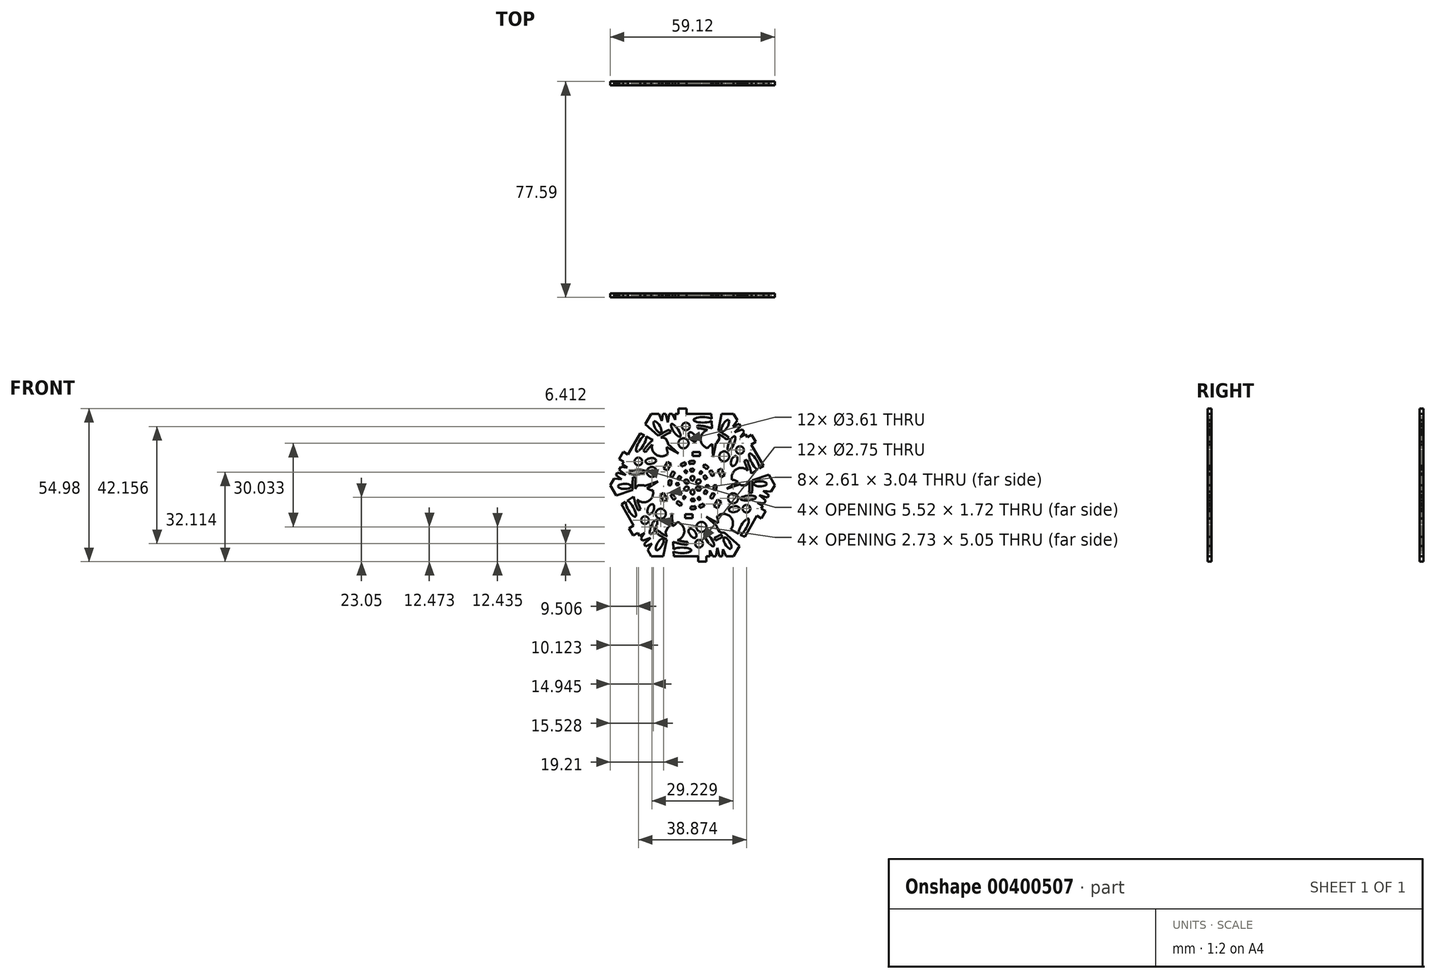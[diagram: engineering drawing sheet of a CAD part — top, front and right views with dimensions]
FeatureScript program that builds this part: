
annotation { "Feature Type Name" : "Feature", "Feature Type Description" : "" }
export const myFeature = defineFeature(function(context is Context, id is Id, definition is map)
    precondition{}
    {
        {
            var Q0;
            Q0=qCreatedBy(makeId("Front.planeOp"),FACE);
            var sketch = newSketch(context, id + "F0", { "sketchPlane" : qUnion([Q0])});
            skLineSegment(sketch, "E0", {"start": v(0, 0) * mm, "end": v(-15.64, -27.08) * mm});
            skLineSegment(sketch, "E1", {"start": v(-29.56, -51.2) * mm, "end": v(4.14, -51.2) * mm});
            skLineSegment(sketch, "E2", {"start": v(29.56, -51.2) * mm, "end": v(17.4, -30.14) * mm});
            skArc(sketch, "E3", {"start": v(-19.34, -33.5) * mm, "mid": v(-6.77, -36.48) * mm, "end": v(-15.64, -27.08) * mm});
            skArc(sketch, "E4", {"start": v(17.4, -30.14) * mm, "mid": v(17.43, -22.72) * mm, "end": v(10.99, -19.03) * mm});
            skLineSegment(sketch, "E5.top", {"start": v(4.14, -54.98) * mm, "end": v(10.05, -54.98) * mm});
            skLineSegment(sketch, "E5.left", {"start": v(4.14, -51.2) * mm, "end": v(4.14, -54.98) * mm});
            skLineSegment(sketch, "E5.right", {"start": v(10.05, -51.2) * mm, "end": v(10.05, -54.98) * mm});
            skLineSegment(sketch, "E6.bottom", {"start": v(-5.32, -20.89) * mm, "end": v(0, -20.89) * mm});
            skLineSegment(sketch, "E6.top", {"start": v(-5.32, -23.85) * mm, "end": v(0, -23.85) * mm});
            skLineSegment(sketch, "E6.left", {"start": v(-5.32, -20.89) * mm, "end": v(-5.32, -23.85) * mm});
            skLineSegment(sketch, "E6.right", {"start": v(0, -20.89) * mm, "end": v(0, -23.85) * mm});
            skLineSegment(sketch, "E7.trimOffspring", {"start": v(-19.34, -33.5) * mm, "end": v(-29.56, -51.2) * mm});
            skLineSegment(sketch, "E8.trimOffspring", {"start": v(10.99, -19.03) * mm, "end": v(0, 0) * mm});
            skLineSegment(sketch, "E9.trimOffspring", {"start": v(10.05, -51.2) * mm, "end": v(29.56, -51.2) * mm});
            skArc(sketch, "E10.1.0", {"start": v(19.34, -33.5) * mm, "mid": v(28.2, -24.1) * mm, "end": v(15.64, -27.08) * mm});
            skLineSegment(sketch, "E10.1.1", {"start": v(15.43, -15.05) * mm, "end": v(18.1, -10.44) * mm});
            skArc(sketch, "E10.1.2", {"start": v(34.8, 0) * mm, "mid": v(28.39, 3.73) * mm, "end": v(21.97, 0) * mm});
            skLineSegment(sketch, "E10.1.3", {"start": v(49.69, -23.9) * mm, "end": v(52.64, -18.79) * mm});
            skLineSegment(sketch, "E10.1.4", {"start": v(59.12, 0) * mm, "end": v(34.8, 0) * mm});
            skLineSegment(sketch, "E10.1.5", {"start": v(29.56, -51.2) * mm, "end": v(46.4, -22.02) * mm});
            skLineSegment(sketch, "E10.1.6", {"start": v(0, 0) * mm, "end": v(15.64, -27.08) * mm});
            skLineSegment(sketch, "E10.1.7", {"start": v(18, -16.53) * mm, "end": v(20.65, -11.92) * mm});
            skLineSegment(sketch, "E10.1.8", {"start": v(19.34, -33.5) * mm, "end": v(29.56, -51.2) * mm});
            skLineSegment(sketch, "E10.1.9", {"start": v(49.37, -16.9) * mm, "end": v(59.12, 0) * mm});
            skLineSegment(sketch, "E10.1.10", {"start": v(21.97, 0) * mm, "end": v(0, 0) * mm});
            skLineSegment(sketch, "E10.1.11", {"start": v(46.4, -22.02) * mm, "end": v(49.69, -23.9) * mm});
            skLineSegment(sketch, "E10.1.12", {"start": v(49.37, -16.9) * mm, "end": v(52.64, -18.79) * mm});
            skLineSegment(sketch, "E10.1.13", {"start": v(15.43, -15.05) * mm, "end": v(18, -16.53) * mm});
            skLineSegment(sketch, "E10.1.14", {"start": v(18.1, -10.44) * mm, "end": v(20.65, -11.92) * mm});
            skArc(sketch, "E10.2.0", {"start": v(38.68, 0) * mm, "mid": v(34.98, 12.37) * mm, "end": v(31.27, 0) * mm});
            skLineSegment(sketch, "E10.2.1", {"start": v(20.75, 5.84) * mm, "end": v(18.1, 10.44) * mm});
            skArc(sketch, "E10.2.2", {"start": v(17.4, 30.14) * mm, "mid": v(10.96, 26.45) * mm, "end": v(10.99, 19.03) * mm});
            skLineSegment(sketch, "E10.2.3", {"start": v(45.55, 31.08) * mm, "end": v(42.6, 36.2) * mm});
            skLineSegment(sketch, "E10.2.4", {"start": v(29.56, 51.2) * mm, "end": v(17.4, 30.14) * mm});
            skLineSegment(sketch, "E10.2.5", {"start": v(59.12, 0) * mm, "end": v(42.27, 29.18) * mm});
            skLineSegment(sketch, "E10.2.6", {"start": v(0, 0) * mm, "end": v(31.27, 0) * mm});
            skLineSegment(sketch, "E10.2.7", {"start": v(23.31, 7.31) * mm, "end": v(20.65, 11.92) * mm});
            skLineSegment(sketch, "E10.2.8", {"start": v(38.68, 0) * mm, "end": v(59.12, 0) * mm});
            skLineSegment(sketch, "E10.2.9", {"start": v(39.32, 34.3) * mm, "end": v(29.56, 51.2) * mm});
            skLineSegment(sketch, "E10.2.10", {"start": v(10.99, 19.03) * mm, "end": v(0, 0) * mm});
            skLineSegment(sketch, "E10.2.11", {"start": v(42.27, 29.18) * mm, "end": v(45.55, 31.08) * mm});
            skLineSegment(sketch, "E10.2.12", {"start": v(39.32, 34.3) * mm, "end": v(42.6, 36.2) * mm});
            skLineSegment(sketch, "E10.2.13", {"start": v(20.75, 5.84) * mm, "end": v(23.31, 7.31) * mm});
            skLineSegment(sketch, "E10.2.14", {"start": v(18.1, 10.44) * mm, "end": v(20.65, 11.92) * mm});
            skArc(sketch, "E10.3.0", {"start": v(19.34, 33.5) * mm, "mid": v(6.77, 36.48) * mm, "end": v(15.64, 27.08) * mm});
            skLineSegment(sketch, "E10.3.1", {"start": v(5.32, 20.89) * mm, "end": v(0, 20.89) * mm});
            skArc(sketch, "E10.3.2", {"start": v(-17.4, 30.14) * mm, "mid": v(-17.43, 22.72) * mm, "end": v(-10.99, 19.03) * mm});
            skLineSegment(sketch, "E10.3.3", {"start": v(-4.14, 54.98) * mm, "end": v(-10.05, 54.98) * mm});
            skLineSegment(sketch, "E10.3.4", {"start": v(-29.56, 51.2) * mm, "end": v(-17.4, 30.14) * mm});
            skLineSegment(sketch, "E10.3.5", {"start": v(29.56, 51.2) * mm, "end": v(-4.14, 51.2) * mm});
            skLineSegment(sketch, "E10.3.6", {"start": v(0, 0) * mm, "end": v(15.64, 27.08) * mm});
            skLineSegment(sketch, "E10.3.7", {"start": v(5.32, 23.85) * mm, "end": v(0, 23.85) * mm});
            skLineSegment(sketch, "E10.3.8", {"start": v(19.34, 33.5) * mm, "end": v(29.56, 51.2) * mm});
            skLineSegment(sketch, "E10.3.9", {"start": v(-10.05, 51.2) * mm, "end": v(-29.56, 51.2) * mm});
            skLineSegment(sketch, "E10.3.10", {"start": v(-10.99, 19.03) * mm, "end": v(0, 0) * mm});
            skLineSegment(sketch, "E10.3.11", {"start": v(-4.14, 51.2) * mm, "end": v(-4.14, 54.98) * mm});
            skLineSegment(sketch, "E10.3.12", {"start": v(-10.05, 51.2) * mm, "end": v(-10.05, 54.98) * mm});
            skLineSegment(sketch, "E10.3.13", {"start": v(5.32, 20.89) * mm, "end": v(5.32, 23.85) * mm});
            skLineSegment(sketch, "E10.3.14", {"start": v(0, 20.89) * mm, "end": v(0, 23.85) * mm});
            skArc(sketch, "E10.4.0", {"start": v(-19.34, 33.5) * mm, "mid": v(-28.2, 24.1) * mm, "end": v(-15.64, 27.08) * mm});
            skLineSegment(sketch, "E10.4.1", {"start": v(-15.43, 15.05) * mm, "end": v(-18.1, 10.44) * mm});
            skArc(sketch, "E10.4.2", {"start": v(-34.8, 0) * mm, "mid": v(-28.39, -3.73) * mm, "end": v(-21.97, 0) * mm});
            skLineSegment(sketch, "E10.4.3", {"start": v(-49.69, 23.9) * mm, "end": v(-52.64, 18.79) * mm});
            skLineSegment(sketch, "E10.4.4", {"start": v(-59.12, 0) * mm, "end": v(-34.8, 0) * mm});
            skLineSegment(sketch, "E10.4.5", {"start": v(-29.56, 51.2) * mm, "end": v(-46.4, 22.02) * mm});
            skLineSegment(sketch, "E10.4.6", {"start": v(0, 0) * mm, "end": v(-15.64, 27.08) * mm});
            skLineSegment(sketch, "E10.4.7", {"start": v(-18, 16.53) * mm, "end": v(-20.65, 11.92) * mm});
            skLineSegment(sketch, "E10.4.8", {"start": v(-19.34, 33.5) * mm, "end": v(-29.56, 51.2) * mm});
            skLineSegment(sketch, "E10.4.9", {"start": v(-49.37, 16.9) * mm, "end": v(-59.12, 0) * mm});
            skLineSegment(sketch, "E10.4.10", {"start": v(-21.97, 0) * mm, "end": v(0, 0) * mm});
            skLineSegment(sketch, "E10.4.11", {"start": v(-46.4, 22.02) * mm, "end": v(-49.69, 23.9) * mm});
            skLineSegment(sketch, "E10.4.12", {"start": v(-49.37, 16.9) * mm, "end": v(-52.64, 18.79) * mm});
            skLineSegment(sketch, "E10.4.13", {"start": v(-15.43, 15.05) * mm, "end": v(-18, 16.53) * mm});
            skLineSegment(sketch, "E10.4.14", {"start": v(-18.1, 10.44) * mm, "end": v(-20.65, 11.92) * mm});
            skArc(sketch, "E10.5.0", {"start": v(-38.68, 0) * mm, "mid": v(-34.98, -12.37) * mm, "end": v(-31.27, 0) * mm});
            skLineSegment(sketch, "E10.5.1", {"start": v(-20.75, -5.84) * mm, "end": v(-18.1, -10.44) * mm});
            skArc(sketch, "E10.5.2", {"start": v(-17.4, -30.14) * mm, "mid": v(-10.96, -26.45) * mm, "end": v(-10.99, -19.03) * mm});
            skLineSegment(sketch, "E10.5.3", {"start": v(-45.55, -31.08) * mm, "end": v(-42.6, -36.2) * mm});
            skLineSegment(sketch, "E10.5.4", {"start": v(-29.56, -51.2) * mm, "end": v(-17.4, -30.14) * mm});
            skLineSegment(sketch, "E10.5.5", {"start": v(-59.12, 0) * mm, "end": v(-42.27, -29.18) * mm});
            skLineSegment(sketch, "E10.5.6", {"start": v(0, 0) * mm, "end": v(-31.27, 0) * mm});
            skLineSegment(sketch, "E10.5.7", {"start": v(-23.31, -7.31) * mm, "end": v(-20.65, -11.92) * mm});
            skLineSegment(sketch, "E10.5.8", {"start": v(-38.68, 0) * mm, "end": v(-59.12, 0) * mm});
            skLineSegment(sketch, "E10.5.9", {"start": v(-39.32, -34.3) * mm, "end": v(-29.56, -51.2) * mm});
            skLineSegment(sketch, "E10.5.10", {"start": v(-10.99, -19.03) * mm, "end": v(0, 0) * mm});
            skLineSegment(sketch, "E10.5.11", {"start": v(-42.27, -29.18) * mm, "end": v(-45.55, -31.08) * mm});
            skLineSegment(sketch, "E10.5.12", {"start": v(-39.32, -34.3) * mm, "end": v(-42.6, -36.2) * mm});
            skLineSegment(sketch, "E10.5.13", {"start": v(-20.75, -5.84) * mm, "end": v(-23.31, -7.31) * mm});
            skLineSegment(sketch, "E10.5.14", {"start": v(-18.1, -10.44) * mm, "end": v(-20.65, -11.92) * mm});
            skPoint(sketch, "E10.center", {"position": v(0, 0) * mm});
            skSolve(sketch);
        }
        {
            var Q0;
            Q0=makeQuery(id+"F0.imprint","IMPRINT",FACE,{"disambiguationData":[TD([[makeQuery(id+"F0.imprint","IMPRINT",EDGE,{"derivedFrom":sQuery(id+"F0.wireOp",EDGE,"E10.4.1")}),1.0]])]});
            var Q1;
            Q1=makeQuery(id+"F0.imprint","IMPRINT",FACE,{"disambiguationData":[TD([[makeQuery(id+"F0.imprint","IMPRINT",EDGE,{"derivedFrom":sQuery(id+"F0.wireOp",EDGE,"E10.1.1")}),1.0]])]});
            var Q2;
            {var subQ0=sQuery(id+"F0.wireOp",EDGE,"E1");Q2=makeQuery(id+"F0.imprint","IMPRINT",FACE,{"disambiguationData":[TD([[makeQuery(id+"F0.imprint","IMPRINT",EDGE,{"derivedFrom":subQ0}),1.0]])]});}
            var Q3;
            Q3=makeQuery(id+"F0.imprint","IMPRINT",FACE,{"disambiguationData":[TD([[makeQuery(id+"F0.imprint","IMPRINT",EDGE,{"derivedFrom":sQuery(id+"F0.wireOp",EDGE,"E10.2.1")}),1.0]])]});
            var Q4;
            Q4=makeQuery(id+"F0.imprint","IMPRINT",FACE,{"disambiguationData":[TD([[makeQuery(id+"F0.imprint","IMPRINT",EDGE,{"derivedFrom":sQuery(id+"F0.wireOp",EDGE,"E10.3.1")}),1.0]])]});
            var Q5;
            {var subQ0=sQuery(id+"F0.wireOp",EDGE,"E10.4.6");var subQ1=sQuery(id+"F0.wireOp",EDGE,"E10.3.2");var subQ2=makeQuery(id+"F0.imprint","INTERSECT",VERTEX,{"derivedFrom":[subQ1,subQ0]});Q5=makeQuery(id+"F0.imprint","IMPRINT",FACE,{"disambiguationData":[TD([[makeQuery(id+"F0.imprint","IMPRINT",EDGE,{"disambiguationData":[TD([[subQ2,1.0]])],"derivedFrom":subQ1}),1.0]])]});}
            var Q6;
            {var subQ0=sQuery(id+"F0.wireOp",EDGE,"E10.3.6");var subQ1=sQuery(id+"F0.wireOp",EDGE,"E10.2.2");var subQ2=makeQuery(id+"F0.imprint","INTERSECT",VERTEX,{"derivedFrom":[subQ1,subQ0]});Q6=makeQuery(id+"F0.imprint","IMPRINT",FACE,{"disambiguationData":[TD([[makeQuery(id+"F0.imprint","IMPRINT",EDGE,{"disambiguationData":[TD([[subQ2,1.0]])],"derivedFrom":subQ1}),1.0]])]});}
            var Q7;
            {var subQ0=sQuery(id+"F0.wireOp",EDGE,"E0");Q7=makeQuery(id+"F0.imprint","IMPRINT",FACE,{"disambiguationData":[TD([[makeQuery(id+"F0.imprint","IMPRINT",EDGE,{"derivedFrom":subQ0}),1.0]])]});}
            var Q8;
            {var subQ0=sQuery(id+"F0.wireOp",EDGE,"E10.1.6");var subQ1=sQuery(id+"F0.wireOp",EDGE,"E4");var subQ2=makeQuery(id+"F0.imprint","INTERSECT",VERTEX,{"derivedFrom":[subQ1,subQ0]});Q8=makeQuery(id+"F0.imprint","IMPRINT",FACE,{"disambiguationData":[TD([[makeQuery(id+"F0.imprint","IMPRINT",EDGE,{"disambiguationData":[TD([[subQ2,1.0]])],"derivedFrom":subQ1}),1.0]])]});}
            var Q9;
            {var subQ0=sQuery(id+"F0.wireOp",EDGE,"E10.2.6");var subQ1=sQuery(id+"F0.wireOp",EDGE,"E10.1.2");var subQ2=makeQuery(id+"F0.imprint","INTERSECT",VERTEX,{"derivedFrom":[subQ1,subQ0]});Q9=makeQuery(id+"F0.imprint","IMPRINT",FACE,{"disambiguationData":[TD([[makeQuery(id+"F0.imprint","IMPRINT",EDGE,{"disambiguationData":[TD([[subQ2,1.0]])],"derivedFrom":subQ1}),1.0]])]});}
            var Q10;
            {var subQ0=sQuery(id+"F0.wireOp",EDGE,"E10.5.6");var subQ1=sQuery(id+"F0.wireOp",EDGE,"E10.4.2");var subQ2=makeQuery(id+"F0.imprint","INTERSECT",VERTEX,{"derivedFrom":[subQ1,subQ0]});Q10=makeQuery(id+"F0.imprint","IMPRINT",FACE,{"disambiguationData":[TD([[makeQuery(id+"F0.imprint","IMPRINT",EDGE,{"disambiguationData":[TD([[subQ2,1.0]])],"derivedFrom":subQ1}),1.0]])]});}
            var Q11;
            {var subQ7=sQuery(id+"F0.wireOp",EDGE,"E0");Q11=makeQuery(id+"F0.imprint","IMPRINT",FACE,{"disambiguationData":[TD([[makeQuery(id+"F0.imprint","IMPRINT",EDGE,{"derivedFrom":subQ7}),-1.0]])]});}
            extrude(context, id + "F1", {"entities" : qUnion([Q0, Q1, Q2, Q3, Q4, Q5, Q6, Q7, Q8, Q9, Q10, Q11]), "depth" : 2.8 * mm});
        }
        {
            var Q0;
            Q0=makeQuery(id+"F1.opExtrude","CAP_FACE",FACE,{"disambiguationData":[OSD([sQuery(id+"F0.wireOp",EDGE,"E1"),sQuery(id+"F0.wireOp",EDGE,"E2"),sQuery(id+"F0.wireOp",EDGE,"E3"),sQuery(id+"F0.wireOp",EDGE,"E4"),sQuery(id+"F0.wireOp",EDGE,"E5.top"),sQuery(id+"F0.wireOp",EDGE,"E5.left"),sQuery(id+"F0.wireOp",EDGE,"E5.right"),sQuery(id+"F0.wireOp",EDGE,"E6.bottom"),sQuery(id+"F0.wireOp",EDGE,"E6.top"),sQuery(id+"F0.wireOp",EDGE,"E6.left"),sQuery(id+"F0.wireOp",EDGE,"E6.right"),sQuery(id+"F0.wireOp",EDGE,"E9.trimOffspring"),sQuery(id+"F0.wireOp",EDGE,"E10.1.0"),sQuery(id+"F0.wireOp",EDGE,"E10.1.1"),sQuery(id+"F0.wireOp",EDGE,"E10.1.2"),sQuery(id+"F0.wireOp",EDGE,"E10.1.3"),sQuery(id+"F0.wireOp",EDGE,"E10.1.4"),sQuery(id+"F0.wireOp",EDGE,"E10.1.5"),sQuery(id+"F0.wireOp",EDGE,"E10.1.7"),sQuery(id+"F0.wireOp",EDGE,"E10.1.9"),sQuery(id+"F0.wireOp",EDGE,"E10.1.11"),sQuery(id+"F0.wireOp",EDGE,"E10.1.12"),sQuery(id+"F0.wireOp",EDGE,"E10.1.13"),sQuery(id+"F0.wireOp",EDGE,"E10.1.14"),sQuery(id+"F0.wireOp",EDGE,"E10.2.0"),sQuery(id+"F0.wireOp",EDGE,"E10.2.1"),sQuery(id+"F0.wireOp",EDGE,"E10.2.2"),sQuery(id+"F0.wireOp",EDGE,"E10.2.3"),sQuery(id+"F0.wireOp",EDGE,"E10.2.4"),sQuery(id+"F0.wireOp",EDGE,"E10.2.5"),sQuery(id+"F0.wireOp",EDGE,"E10.2.7"),sQuery(id+"F0.wireOp",EDGE,"E10.2.9"),sQuery(id+"F0.wireOp",EDGE,"E10.2.11"),sQuery(id+"F0.wireOp",EDGE,"E10.2.12"),sQuery(id+"F0.wireOp",EDGE,"E10.2.13"),sQuery(id+"F0.wireOp",EDGE,"E10.2.14"),sQuery(id+"F0.wireOp",EDGE,"E10.3.0"),sQuery(id+"F0.wireOp",EDGE,"E10.3.1"),sQuery(id+"F0.wireOp",EDGE,"E10.3.2"),sQuery(id+"F0.wireOp",EDGE,"E10.3.3"),sQuery(id+"F0.wireOp",EDGE,"E10.3.4"),sQuery(id+"F0.wireOp",EDGE,"E10.3.5"),sQuery(id+"F0.wireOp",EDGE,"E10.3.7"),sQuery(id+"F0.wireOp",EDGE,"E10.3.9"),sQuery(id+"F0.wireOp",EDGE,"E10.3.11"),sQuery(id+"F0.wireOp",EDGE,"E10.3.12"),sQuery(id+"F0.wireOp",EDGE,"E10.3.13"),sQuery(id+"F0.wireOp",EDGE,"E10.3.14"),sQuery(id+"F0.wireOp",EDGE,"E10.4.0"),sQuery(id+"F0.wireOp",EDGE,"E10.4.1"),sQuery(id+"F0.wireOp",EDGE,"E10.4.2"),sQuery(id+"F0.wireOp",EDGE,"E10.4.3"),sQuery(id+"F0.wireOp",EDGE,"E10.4.4"),sQuery(id+"F0.wireOp",EDGE,"E10.4.5"),sQuery(id+"F0.wireOp",EDGE,"E10.4.7"),sQuery(id+"F0.wireOp",EDGE,"E10.4.9"),sQuery(id+"F0.wireOp",EDGE,"E10.4.11"),sQuery(id+"F0.wireOp",EDGE,"E10.4.12"),sQuery(id+"F0.wireOp",EDGE,"E10.4.13"),sQuery(id+"F0.wireOp",EDGE,"E10.4.14"),sQuery(id+"F0.wireOp",EDGE,"E10.5.0"),sQuery(id+"F0.wireOp",EDGE,"E10.5.1"),sQuery(id+"F0.wireOp",EDGE,"E10.5.2"),sQuery(id+"F0.wireOp",EDGE,"E10.5.3"),sQuery(id+"F0.wireOp",EDGE,"E10.5.4"),sQuery(id+"F0.wireOp",EDGE,"E10.5.5"),sQuery(id+"F0.wireOp",EDGE,"E10.5.7"),sQuery(id+"F0.wireOp",EDGE,"E10.5.9"),sQuery(id+"F0.wireOp",EDGE,"E10.5.11"),sQuery(id+"F0.wireOp",EDGE,"E10.5.12"),sQuery(id+"F0.wireOp",EDGE,"E10.5.13"),sQuery(id+"F0.wireOp",EDGE,"E10.5.14")])],"isStart":false});
            var sketch = newSketch(context, id + "F2", { "sketchPlane" : qUnion([Q0])});
            skCircle(sketch, "E11", {"center": v(-22.79, -20.6) * mm, "radius": 3.61 * mm});
            skCircle(sketch, "E12.1.0", {"center": v(6.44, -30.03) * mm, "radius": 3.61 * mm});
            skCircle(sketch, "E12.2.0", {"center": v(29.23, -9.44) * mm, "radius": 3.61 * mm});
            skCircle(sketch, "E12.3.0", {"center": v(22.79, 20.6) * mm, "radius": 3.61 * mm});
            skCircle(sketch, "E12.4.0", {"center": v(-6.44, 30.03) * mm, "radius": 3.61 * mm});
            skCircle(sketch, "E12.5.0", {"center": v(-29.23, 9.44) * mm, "radius": 3.61 * mm});
            skPoint(sketch, "E12.center", {"position": v(0, 0) * mm});
            skSolve(sketch);
        }
        {
            var Q0;
            Q0 = qSketchRegion(id + "F2", true);
            extrude(context, id + "F3", {"entities" : qUnion([Q0]), "operationType" : NewBodyOperationType.REMOVE, "oppositeDirection" : true, "depth" : 25.4 * mm});
        }
        {
            var Q0;
            Q0=makeQuery(id+"F1.opExtrude","CAP_FACE",FACE,{"disambiguationData":[OSD([sQuery(id+"F0.wireOp",EDGE,"E1"),sQuery(id+"F0.wireOp",EDGE,"E2"),sQuery(id+"F0.wireOp",EDGE,"E3"),sQuery(id+"F0.wireOp",EDGE,"E4"),sQuery(id+"F0.wireOp",EDGE,"E5.top"),sQuery(id+"F0.wireOp",EDGE,"E5.left"),sQuery(id+"F0.wireOp",EDGE,"E5.right"),sQuery(id+"F0.wireOp",EDGE,"E6.bottom"),sQuery(id+"F0.wireOp",EDGE,"E6.top"),sQuery(id+"F0.wireOp",EDGE,"E6.left"),sQuery(id+"F0.wireOp",EDGE,"E6.right"),sQuery(id+"F0.wireOp",EDGE,"E9.trimOffspring"),sQuery(id+"F0.wireOp",EDGE,"E10.1.0"),sQuery(id+"F0.wireOp",EDGE,"E10.1.1"),sQuery(id+"F0.wireOp",EDGE,"E10.1.2"),sQuery(id+"F0.wireOp",EDGE,"E10.1.3"),sQuery(id+"F0.wireOp",EDGE,"E10.1.4"),sQuery(id+"F0.wireOp",EDGE,"E10.1.5"),sQuery(id+"F0.wireOp",EDGE,"E10.1.7"),sQuery(id+"F0.wireOp",EDGE,"E10.1.9"),sQuery(id+"F0.wireOp",EDGE,"E10.1.11"),sQuery(id+"F0.wireOp",EDGE,"E10.1.12"),sQuery(id+"F0.wireOp",EDGE,"E10.1.13"),sQuery(id+"F0.wireOp",EDGE,"E10.1.14"),sQuery(id+"F0.wireOp",EDGE,"E10.2.0"),sQuery(id+"F0.wireOp",EDGE,"E10.2.1"),sQuery(id+"F0.wireOp",EDGE,"E10.2.2"),sQuery(id+"F0.wireOp",EDGE,"E10.2.3"),sQuery(id+"F0.wireOp",EDGE,"E10.2.4"),sQuery(id+"F0.wireOp",EDGE,"E10.2.5"),sQuery(id+"F0.wireOp",EDGE,"E10.2.7"),sQuery(id+"F0.wireOp",EDGE,"E10.2.9"),sQuery(id+"F0.wireOp",EDGE,"E10.2.11"),sQuery(id+"F0.wireOp",EDGE,"E10.2.12"),sQuery(id+"F0.wireOp",EDGE,"E10.2.13"),sQuery(id+"F0.wireOp",EDGE,"E10.2.14"),sQuery(id+"F0.wireOp",EDGE,"E10.3.0"),sQuery(id+"F0.wireOp",EDGE,"E10.3.1"),sQuery(id+"F0.wireOp",EDGE,"E10.3.2"),sQuery(id+"F0.wireOp",EDGE,"E10.3.3"),sQuery(id+"F0.wireOp",EDGE,"E10.3.4"),sQuery(id+"F0.wireOp",EDGE,"E10.3.5"),sQuery(id+"F0.wireOp",EDGE,"E10.3.7"),sQuery(id+"F0.wireOp",EDGE,"E10.3.9"),sQuery(id+"F0.wireOp",EDGE,"E10.3.11"),sQuery(id+"F0.wireOp",EDGE,"E10.3.12"),sQuery(id+"F0.wireOp",EDGE,"E10.3.13"),sQuery(id+"F0.wireOp",EDGE,"E10.3.14"),sQuery(id+"F0.wireOp",EDGE,"E10.4.0"),sQuery(id+"F0.wireOp",EDGE,"E10.4.1"),sQuery(id+"F0.wireOp",EDGE,"E10.4.2"),sQuery(id+"F0.wireOp",EDGE,"E10.4.3"),sQuery(id+"F0.wireOp",EDGE,"E10.4.4"),sQuery(id+"F0.wireOp",EDGE,"E10.4.5"),sQuery(id+"F0.wireOp",EDGE,"E10.4.7"),sQuery(id+"F0.wireOp",EDGE,"E10.4.9"),sQuery(id+"F0.wireOp",EDGE,"E10.4.11"),sQuery(id+"F0.wireOp",EDGE,"E10.4.12"),sQuery(id+"F0.wireOp",EDGE,"E10.4.13"),sQuery(id+"F0.wireOp",EDGE,"E10.4.14"),sQuery(id+"F0.wireOp",EDGE,"E10.5.0"),sQuery(id+"F0.wireOp",EDGE,"E10.5.1"),sQuery(id+"F0.wireOp",EDGE,"E10.5.2"),sQuery(id+"F0.wireOp",EDGE,"E10.5.3"),sQuery(id+"F0.wireOp",EDGE,"E10.5.4"),sQuery(id+"F0.wireOp",EDGE,"E10.5.5"),sQuery(id+"F0.wireOp",EDGE,"E10.5.7"),sQuery(id+"F0.wireOp",EDGE,"E10.5.9"),sQuery(id+"F0.wireOp",EDGE,"E10.5.11"),sQuery(id+"F0.wireOp",EDGE,"E10.5.12"),sQuery(id+"F0.wireOp",EDGE,"E10.5.13"),sQuery(id+"F0.wireOp",EDGE,"E10.5.14")])],"isStart":false});
            var sketch = newSketch(context, id + "F4", { "sketchPlane" : qUnion([Q0])});
            skLineSegment(sketch, "E13", {"start": v(-60.1, -9.23) * mm, "end": v(-24.79, 2.75) * mm});
            skLineSegment(sketch, "E14", {"start": v(-24.79, 2.75) * mm, "end": v(-55.88, -16.93) * mm});
            skLineSegment(sketch, "E15", {"start": v(-55.88, -16.93) * mm, "end": v(-60.1, -9.23) * mm});
            skLineSegment(sketch, "E16", {"start": v(-42.6, -39.03) * mm, "end": v(-34.41, -34.3) * mm});
            skLineSegment(sketch, "E17", {"start": v(-34.41, -34.3) * mm, "end": v(-39.32, -41.38) * mm});
            skLineSegment(sketch, "E18", {"start": v(-39.32, -41.38) * mm, "end": v(-30.23, -37.99) * mm});
            skLineSegment(sketch, "E19", {"start": v(-30.23, -37.99) * mm, "end": v(-38.68, -46.15) * mm});
            skLineSegment(sketch, "E20", {"start": v(-38.68, -46.15) * mm, "end": v(-29.02, -42.08) * mm});
            skLineSegment(sketch, "E21", {"start": v(-29.02, -42.08) * mm, "end": v(-34.8, -49.92) * mm});
            skLineSegment(sketch, "E22", {"start": v(-34.8, -49.92) * mm, "end": v(-42.27, -49.92) * mm});
            skLineSegment(sketch, "E23", {"start": v(-42.27, -49.92) * mm, "end": v(-42.6, -39.03) * mm});
            skLineSegment(sketch, "E24.1.0", {"start": v(16.18, -54.74) * mm, "end": v(17.78, -45.17) * mm});
            skLineSegment(sketch, "E24.1.1", {"start": v(12.5, -46.95) * mm, "end": v(16.18, -54.74) * mm});
            skLineSegment(sketch, "E24.1.2", {"start": v(12.5, -56.4) * mm, "end": v(12.5, -46.95) * mm});
            skLineSegment(sketch, "E24.1.3", {"start": v(-13.28, -56.86) * mm, "end": v(-22.05, -56.65) * mm});
            skLineSegment(sketch, "E24.1.4", {"start": v(-22.05, -56.65) * mm, "end": v(-14.77, -20.1) * mm});
            skLineSegment(sketch, "E24.1.5", {"start": v(-14.77, -20.1) * mm, "end": v(-13.28, -56.86) * mm});
            skLineSegment(sketch, "E24.1.6", {"start": v(20.63, -56.58) * mm, "end": v(21.93, -46.17) * mm});
            skLineSegment(sketch, "E24.1.7", {"start": v(21.93, -46.17) * mm, "end": v(25.83, -55.1) * mm});
            skLineSegment(sketch, "E24.1.8", {"start": v(17.78, -45.17) * mm, "end": v(20.63, -56.58) * mm});
            skLineSegment(sketch, "E24.1.9", {"start": v(25.83, -55.1) * mm, "end": v(22.1, -61.57) * mm});
            skLineSegment(sketch, "E24.1.10", {"start": v(22.1, -61.57) * mm, "end": v(12.5, -56.4) * mm});
            skLineSegment(sketch, "E24.2.0", {"start": v(55.5, -13.36) * mm, "end": v(48.01, -7.19) * mm});
            skLineSegment(sketch, "E24.2.1", {"start": v(46.91, -12.65) * mm, "end": v(55.5, -13.36) * mm});
            skLineSegment(sketch, "E24.2.2", {"start": v(55.1, -17.37) * mm, "end": v(46.91, -12.65) * mm});
            skLineSegment(sketch, "E24.2.3", {"start": v(42.6, -39.93) * mm, "end": v(38.04, -47.43) * mm});
            skLineSegment(sketch, "E24.2.4", {"start": v(38.04, -47.43) * mm, "end": v(10.01, -22.84) * mm});
            skLineSegment(sketch, "E24.2.5", {"start": v(10.01, -22.84) * mm, "end": v(42.6, -39.93) * mm});
            skLineSegment(sketch, "E24.2.6", {"start": v(59.31, -10.42) * mm, "end": v(50.95, -4.1) * mm});
            skLineSegment(sketch, "E24.2.7", {"start": v(50.95, -4.1) * mm, "end": v(60.63, -5.18) * mm});
            skLineSegment(sketch, "E24.2.8", {"start": v(48.01, -7.19) * mm, "end": v(59.31, -10.42) * mm});
            skLineSegment(sketch, "E24.2.9", {"start": v(60.63, -5.18) * mm, "end": v(64.37, -11.65) * mm});
            skLineSegment(sketch, "E24.2.10", {"start": v(64.37, -11.65) * mm, "end": v(55.1, -17.37) * mm});
            skLineSegment(sketch, "E24.3.0", {"start": v(39.32, 41.38) * mm, "end": v(30.23, 37.99) * mm});
            skLineSegment(sketch, "E24.3.1", {"start": v(34.41, 34.3) * mm, "end": v(39.32, 41.38) * mm});
            skLineSegment(sketch, "E24.3.2", {"start": v(42.6, 39.03) * mm, "end": v(34.41, 34.3) * mm});
            skLineSegment(sketch, "E24.3.3", {"start": v(55.88, 16.93) * mm, "end": v(60.1, 9.23) * mm});
            skLineSegment(sketch, "E24.3.4", {"start": v(60.1, 9.23) * mm, "end": v(24.79, -2.75) * mm});
            skLineSegment(sketch, "E24.3.5", {"start": v(24.79, -2.75) * mm, "end": v(55.88, 16.93) * mm});
            skLineSegment(sketch, "E24.3.6", {"start": v(38.68, 46.15) * mm, "end": v(29.02, 42.08) * mm});
            skLineSegment(sketch, "E24.3.7", {"start": v(29.02, 42.08) * mm, "end": v(34.8, 49.92) * mm});
            skLineSegment(sketch, "E24.3.8", {"start": v(30.23, 37.99) * mm, "end": v(38.68, 46.15) * mm});
            skLineSegment(sketch, "E24.3.9", {"start": v(34.8, 49.92) * mm, "end": v(42.27, 49.92) * mm});
            skLineSegment(sketch, "E24.3.10", {"start": v(42.27, 49.92) * mm, "end": v(42.6, 39.03) * mm});
            skLineSegment(sketch, "E24.4.0", {"start": v(-16.18, 54.74) * mm, "end": v(-17.78, 45.17) * mm});
            skLineSegment(sketch, "E24.4.1", {"start": v(-12.5, 46.95) * mm, "end": v(-16.18, 54.74) * mm});
            skLineSegment(sketch, "E24.4.2", {"start": v(-12.5, 56.4) * mm, "end": v(-12.5, 46.95) * mm});
            skLineSegment(sketch, "E24.4.3", {"start": v(13.28, 56.86) * mm, "end": v(22.05, 56.65) * mm});
            skLineSegment(sketch, "E24.4.4", {"start": v(22.05, 56.65) * mm, "end": v(14.77, 20.1) * mm});
            skLineSegment(sketch, "E24.4.5", {"start": v(14.77, 20.1) * mm, "end": v(13.28, 56.86) * mm});
            skLineSegment(sketch, "E24.4.6", {"start": v(-20.63, 56.58) * mm, "end": v(-21.93, 46.17) * mm});
            skLineSegment(sketch, "E24.4.7", {"start": v(-21.93, 46.17) * mm, "end": v(-25.83, 55.1) * mm});
            skLineSegment(sketch, "E24.4.8", {"start": v(-17.78, 45.17) * mm, "end": v(-20.63, 56.58) * mm});
            skLineSegment(sketch, "E24.4.9", {"start": v(-25.83, 55.1) * mm, "end": v(-22.1, 61.57) * mm});
            skLineSegment(sketch, "E24.4.10", {"start": v(-22.1, 61.57) * mm, "end": v(-12.5, 56.4) * mm});
            skLineSegment(sketch, "E24.5.0", {"start": v(-55.5, 13.36) * mm, "end": v(-48.01, 7.19) * mm});
            skLineSegment(sketch, "E24.5.1", {"start": v(-46.91, 12.65) * mm, "end": v(-55.5, 13.36) * mm});
            skLineSegment(sketch, "E24.5.2", {"start": v(-55.1, 17.37) * mm, "end": v(-46.91, 12.65) * mm});
            skLineSegment(sketch, "E24.5.3", {"start": v(-42.6, 39.93) * mm, "end": v(-38.04, 47.43) * mm});
            skLineSegment(sketch, "E24.5.4", {"start": v(-38.04, 47.43) * mm, "end": v(-10.01, 22.84) * mm});
            skLineSegment(sketch, "E24.5.5", {"start": v(-10.01, 22.84) * mm, "end": v(-42.6, 39.93) * mm});
            skLineSegment(sketch, "E24.5.6", {"start": v(-59.31, 10.42) * mm, "end": v(-50.95, 4.1) * mm});
            skLineSegment(sketch, "E24.5.7", {"start": v(-50.95, 4.1) * mm, "end": v(-60.63, 5.18) * mm});
            skLineSegment(sketch, "E24.5.8", {"start": v(-48.01, 7.19) * mm, "end": v(-59.31, 10.42) * mm});
            skLineSegment(sketch, "E24.5.9", {"start": v(-60.63, 5.18) * mm, "end": v(-64.37, 11.65) * mm});
            skLineSegment(sketch, "E24.5.10", {"start": v(-64.37, 11.65) * mm, "end": v(-55.1, 17.37) * mm});
            skPoint(sketch, "E24.center", {"position": v(0, 0) * mm});
            skSolve(sketch);
        }
        {
            var Q0;
            Q0 = qSketchRegion(id + "F4", true);
            extrude(context, id + "F5", {"entities" : qUnion([Q0]), "operationType" : NewBodyOperationType.REMOVE, "oppositeDirection" : true, "depth" : 25.4 * mm});
        }
        {
            var Q0;
            Q0=makeQuery(id+"F1.opExtrude","CAP_FACE",FACE,{"disambiguationData":[OSD([sQuery(id+"F0.wireOp",EDGE,"E1"),sQuery(id+"F0.wireOp",EDGE,"E2"),sQuery(id+"F0.wireOp",EDGE,"E3"),sQuery(id+"F0.wireOp",EDGE,"E4"),sQuery(id+"F0.wireOp",EDGE,"E5.top"),sQuery(id+"F0.wireOp",EDGE,"E5.left"),sQuery(id+"F0.wireOp",EDGE,"E5.right"),sQuery(id+"F0.wireOp",EDGE,"E6.bottom"),sQuery(id+"F0.wireOp",EDGE,"E6.top"),sQuery(id+"F0.wireOp",EDGE,"E6.left"),sQuery(id+"F0.wireOp",EDGE,"E6.right"),sQuery(id+"F0.wireOp",EDGE,"E9.trimOffspring"),sQuery(id+"F0.wireOp",EDGE,"E10.1.0"),sQuery(id+"F0.wireOp",EDGE,"E10.1.1"),sQuery(id+"F0.wireOp",EDGE,"E10.1.2"),sQuery(id+"F0.wireOp",EDGE,"E10.1.3"),sQuery(id+"F0.wireOp",EDGE,"E10.1.4"),sQuery(id+"F0.wireOp",EDGE,"E10.1.5"),sQuery(id+"F0.wireOp",EDGE,"E10.1.7"),sQuery(id+"F0.wireOp",EDGE,"E10.1.9"),sQuery(id+"F0.wireOp",EDGE,"E10.1.11"),sQuery(id+"F0.wireOp",EDGE,"E10.1.12"),sQuery(id+"F0.wireOp",EDGE,"E10.1.13"),sQuery(id+"F0.wireOp",EDGE,"E10.1.14"),sQuery(id+"F0.wireOp",EDGE,"E10.2.0"),sQuery(id+"F0.wireOp",EDGE,"E10.2.1"),sQuery(id+"F0.wireOp",EDGE,"E10.2.2"),sQuery(id+"F0.wireOp",EDGE,"E10.2.3"),sQuery(id+"F0.wireOp",EDGE,"E10.2.4"),sQuery(id+"F0.wireOp",EDGE,"E10.2.5"),sQuery(id+"F0.wireOp",EDGE,"E10.2.7"),sQuery(id+"F0.wireOp",EDGE,"E10.2.9"),sQuery(id+"F0.wireOp",EDGE,"E10.2.11"),sQuery(id+"F0.wireOp",EDGE,"E10.2.12"),sQuery(id+"F0.wireOp",EDGE,"E10.2.13"),sQuery(id+"F0.wireOp",EDGE,"E10.2.14"),sQuery(id+"F0.wireOp",EDGE,"E10.3.0"),sQuery(id+"F0.wireOp",EDGE,"E10.3.1"),sQuery(id+"F0.wireOp",EDGE,"E10.3.2"),sQuery(id+"F0.wireOp",EDGE,"E10.3.3"),sQuery(id+"F0.wireOp",EDGE,"E10.3.4"),sQuery(id+"F0.wireOp",EDGE,"E10.3.5"),sQuery(id+"F0.wireOp",EDGE,"E10.3.7"),sQuery(id+"F0.wireOp",EDGE,"E10.3.9"),sQuery(id+"F0.wireOp",EDGE,"E10.3.11"),sQuery(id+"F0.wireOp",EDGE,"E10.3.12"),sQuery(id+"F0.wireOp",EDGE,"E10.3.13"),sQuery(id+"F0.wireOp",EDGE,"E10.3.14"),sQuery(id+"F0.wireOp",EDGE,"E10.4.0"),sQuery(id+"F0.wireOp",EDGE,"E10.4.1"),sQuery(id+"F0.wireOp",EDGE,"E10.4.2"),sQuery(id+"F0.wireOp",EDGE,"E10.4.3"),sQuery(id+"F0.wireOp",EDGE,"E10.4.4"),sQuery(id+"F0.wireOp",EDGE,"E10.4.5"),sQuery(id+"F0.wireOp",EDGE,"E10.4.7"),sQuery(id+"F0.wireOp",EDGE,"E10.4.9"),sQuery(id+"F0.wireOp",EDGE,"E10.4.11"),sQuery(id+"F0.wireOp",EDGE,"E10.4.12"),sQuery(id+"F0.wireOp",EDGE,"E10.4.13"),sQuery(id+"F0.wireOp",EDGE,"E10.4.14"),sQuery(id+"F0.wireOp",EDGE,"E10.5.0"),sQuery(id+"F0.wireOp",EDGE,"E10.5.1"),sQuery(id+"F0.wireOp",EDGE,"E10.5.2"),sQuery(id+"F0.wireOp",EDGE,"E10.5.3"),sQuery(id+"F0.wireOp",EDGE,"E10.5.4"),sQuery(id+"F0.wireOp",EDGE,"E10.5.5"),sQuery(id+"F0.wireOp",EDGE,"E10.5.7"),sQuery(id+"F0.wireOp",EDGE,"E10.5.9"),sQuery(id+"F0.wireOp",EDGE,"E10.5.11"),sQuery(id+"F0.wireOp",EDGE,"E10.5.12"),sQuery(id+"F0.wireOp",EDGE,"E10.5.13"),sQuery(id+"F0.wireOp",EDGE,"E10.5.14")])],"isStart":false});
            var sketch = newSketch(context, id + "F6", { "sketchPlane" : qUnion([Q0])});
            skArc(sketch, "E25", {"start": v(-0.85, -9.76) * mm, "mid": v(0.27, -9.8) * mm, "end": v(1.4, -9.7) * mm});
            skArc(sketch, "E26", {"start": v(4.47, -10.8) * mm, "mid": v(5.17, -10.48) * mm, "end": v(5.84, -10.12) * mm});
            skArc(sketch, "E27", {"start": v(-1.33, -15.26) * mm, "mid": v(0.43, -15.31) * mm, "end": v(2.18, -15.16) * mm});
            skArc(sketch, "E28", {"start": v(-1.5, -17.25) * mm, "mid": v(0.48, -17.3) * mm, "end": v(2.46, -17.14) * mm});
            skArc(sketch, "E29", {"start": v(-26.26, -34.19) * mm, "mid": v(-15.62, -40.17) * mm, "end": v(-3.74, -42.94) * mm});
            skArc(sketch, "E30", {"start": v(-25.01, -32.57) * mm, "mid": v(-14.88, -38.27) * mm, "end": v(-3.56, -40.9) * mm});
            skLineSegment(sketch, "E31", {"start": v(-0.85, -9.76) * mm, "end": v(-1.01, -11.64) * mm});
            skLineSegment(sketch, "E32", {"start": v(16.48, -39.83) * mm, "end": v(15.7, -37.95) * mm});
            skLineSegment(sketch, "E33.trimOffspring", {"start": v(-1.33, -15.26) * mm, "end": v(-1.5, -17.25) * mm});
            skLineSegment(sketch, "E34.trimOffspring", {"start": v(1.66, -11.57) * mm, "end": v(1.4, -9.7) * mm});
            skArc(sketch, "E35.trimOffspring", {"start": v(-1.01, -11.64) * mm, "mid": v(0.33, -11.68) * mm, "end": v(1.66, -11.57) * mm});
            skArc(sketch, "E36.trimOffspring", {"start": v(3.75, -9.05) * mm, "mid": v(4.33, -8.79) * mm, "end": v(4.9, -8.48) * mm});
            skArc(sketch, "E37.trimOffspring", {"start": v(5.35, -16.47) * mm, "mid": v(7.04, -15.82) * mm, "end": v(8.66, -15) * mm});
            skArc(sketch, "E38.trimOffspring", {"start": v(4.74, -14.57) * mm, "mid": v(6.23, -14) * mm, "end": v(7.66, -13.27) * mm});
            skLineSegment(sketch, "E39.trimOffspring", {"start": v(-3.56, -40.9) * mm, "end": v(-3.74, -42.94) * mm});
            skLineSegment(sketch, "E40.trimOffspring", {"start": v(2.46, -17.14) * mm, "end": v(2.18, -15.16) * mm});
            skLineSegment(sketch, "E41.trimOffspring", {"start": v(5.84, -10.12) * mm, "end": v(4.9, -8.48) * mm});
            skLineSegment(sketch, "E42.trimOffspring", {"start": v(4.47, -10.8) * mm, "end": v(3.75, -9.05) * mm});
            skLineSegment(sketch, "E43.trimOffspring", {"start": v(4.74, -14.57) * mm, "end": v(5.35, -16.47) * mm});
            skLineSegment(sketch, "E44.trimOffspring", {"start": v(8.66, -15) * mm, "end": v(7.66, -13.27) * mm});
            skArc(sketch, "E45.trimOffspring", {"start": v(15.7, -37.95) * mm, "mid": v(18.15, -36.83) * mm, "end": v(20.53, -35.56) * mm});
            skArc(sketch, "E46.trimOffspring", {"start": v(16.48, -39.83) * mm, "mid": v(19.06, -38.66) * mm, "end": v(21.55, -37.33) * mm});
            skArc(sketch, "E47.1.3", {"start": v(14.98, -3.18) * mm, "mid": v(15.23, -1.6) * mm, "end": v(15.32, 0) * mm});
            skArc(sketch, "E47.1.5", {"start": v(12.55, -8.78) * mm, "mid": v(13.47, -7.29) * mm, "end": v(14.22, -5.7) * mm});
            skLineSegment(sketch, "E47.1.6", {"start": v(16.07, -6.44) * mm, "end": v(14.22, -5.7) * mm});
            skLineSegment(sketch, "E47.1.7", {"start": v(20.53, -35.56) * mm, "end": v(21.55, -37.33) * mm});
            skArc(sketch, "E47.1.8", {"start": v(16.94, -3.6) * mm, "mid": v(17.22, -1.8) * mm, "end": v(17.31, 0) * mm});
            skLineSegment(sketch, "E47.1.10", {"start": v(42.73, -5.64) * mm, "end": v(40.71, -5.38) * mm});
            skLineSegment(sketch, "E47.1.12", {"start": v(14.98, -3.18) * mm, "end": v(16.94, -3.6) * mm});
            skArc(sketch, "E47.1.13", {"start": v(14.19, -9.93) * mm, "mid": v(15.23, -8.24) * mm, "end": v(16.07, -6.44) * mm});
            skLineSegment(sketch, "E47.1.14", {"start": v(17.31, 0) * mm, "end": v(15.32, 0) * mm});
            skLineSegment(sketch, "E47.1.15", {"start": v(12.55, -8.78) * mm, "end": v(14.19, -9.93) * mm});
            skLineSegment(sketch, "E47.1.16", {"start": v(10.85, -4.35) * mm, "end": v(9.1, -3.64) * mm});
            skArc(sketch, "E47.1.17", {"start": v(8.03, -5.62) * mm, "mid": v(8.62, -4.66) * mm, "end": v(9.1, -3.64) * mm});
            skArc(sketch, "E47.1.18", {"start": v(9.58, -6.7) * mm, "mid": v(10.28, -5.56) * mm, "end": v(10.85, -4.35) * mm});
            skLineSegment(sketch, "E47.1.19", {"start": v(11.69, 0) * mm, "end": v(9.8, 0) * mm});
            skArc(sketch, "E47.1.20", {"start": v(11.59, -1.53) * mm, "mid": v(11.66, -0.77) * mm, "end": v(11.69, 0) * mm});
            skArc(sketch, "E47.1.21", {"start": v(9.71, -1.28) * mm, "mid": v(9.78, -0.64) * mm, "end": v(9.8, 0) * mm});
            skLineSegment(sketch, "E47.1.22", {"start": v(8.03, -5.62) * mm, "end": v(9.58, -6.7) * mm});
            skLineSegment(sketch, "E47.1.23", {"start": v(11.59, -1.53) * mm, "end": v(9.71, -1.28) * mm});
            skArc(sketch, "E47.2.0", {"start": v(42.73, -5.64) * mm, "mid": v(42.6, 6.56) * mm, "end": v(39.06, 18.23) * mm});
            skArc(sketch, "E47.2.1", {"start": v(40.71, -5.38) * mm, "mid": v(40.59, 6.25) * mm, "end": v(37.21, 17.37) * mm});
            skArc(sketch, "E47.2.3", {"start": v(10.25, 11.38) * mm, "mid": v(9, 12.4) * mm, "end": v(7.66, 13.27) * mm});
            skArc(sketch, "E47.2.5", {"start": v(13.88, 6.48) * mm, "mid": v(13.05, 8.03) * mm, "end": v(12.04, 9.47) * mm});
            skLineSegment(sketch, "E47.2.6", {"start": v(13.61, 10.7) * mm, "end": v(12.04, 9.47) * mm});
            skArc(sketch, "E47.2.8", {"start": v(11.58, 12.87) * mm, "mid": v(10.18, 14) * mm, "end": v(8.66, 15) * mm});
            skLineSegment(sketch, "E47.2.10", {"start": v(26.26, 34.19) * mm, "end": v(25.01, 32.57) * mm});
            skLineSegment(sketch, "E47.2.11", {"start": v(37.21, 17.37) * mm, "end": v(39.06, 18.23) * mm});
            skLineSegment(sketch, "E47.2.12", {"start": v(10.25, 11.38) * mm, "end": v(11.58, 12.87) * mm});
            skArc(sketch, "E47.2.13", {"start": v(15.69, 7.32) * mm, "mid": v(14.75, 9.07) * mm, "end": v(13.61, 10.7) * mm});
            skLineSegment(sketch, "E47.2.14", {"start": v(8.66, 15) * mm, "end": v(7.66, 13.27) * mm});
            skLineSegment(sketch, "E47.2.15", {"start": v(13.88, 6.48) * mm, "end": v(15.69, 7.32) * mm});
            skLineSegment(sketch, "E47.2.16", {"start": v(9.19, 7.22) * mm, "end": v(7.7, 6.05) * mm});
            skArc(sketch, "E47.2.17", {"start": v(8.88, 4.14) * mm, "mid": v(8.34, 5.13) * mm, "end": v(7.7, 6.05) * mm});
            skArc(sketch, "E47.2.18", {"start": v(10.6, 4.94) * mm, "mid": v(9.96, 6.12) * mm, "end": v(9.19, 7.22) * mm});
            skLineSegment(sketch, "E47.2.19", {"start": v(5.84, 10.12) * mm, "end": v(4.9, 8.48) * mm});
            skArc(sketch, "E47.2.20", {"start": v(7.12, 9.27) * mm, "mid": v(6.5, 9.72) * mm, "end": v(5.84, 10.12) * mm});
            skArc(sketch, "E47.2.21", {"start": v(5.97, 7.77) * mm, "mid": v(5.44, 8.14) * mm, "end": v(4.9, 8.48) * mm});
            skLineSegment(sketch, "E47.2.22", {"start": v(8.88, 4.14) * mm, "end": v(10.6, 4.94) * mm});
            skLineSegment(sketch, "E47.2.23", {"start": v(7.12, 9.27) * mm, "end": v(5.97, 7.77) * mm});
            skArc(sketch, "E47.3.0", {"start": v(26.26, 34.19) * mm, "mid": v(15.62, 40.17) * mm, "end": v(3.74, 42.94) * mm});
            skArc(sketch, "E47.3.1", {"start": v(25.01, 32.57) * mm, "mid": v(14.88, 38.27) * mm, "end": v(3.56, 40.9) * mm});
            skArc(sketch, "E47.3.3", {"start": v(-4.74, 14.57) * mm, "mid": v(-6.23, 14) * mm, "end": v(-7.66, 13.27) * mm});
            skArc(sketch, "E47.3.5", {"start": v(1.33, 15.26) * mm, "mid": v(-0.43, 15.31) * mm, "end": v(-2.18, 15.16) * mm});
            skLineSegment(sketch, "E47.3.6", {"start": v(-2.46, 17.14) * mm, "end": v(-2.18, 15.16) * mm});
            skArc(sketch, "E47.3.8", {"start": v(-5.35, 16.47) * mm, "mid": v(-7.04, 15.82) * mm, "end": v(-8.66, 15) * mm});
            skLineSegment(sketch, "E47.3.10", {"start": v(-16.48, 39.83) * mm, "end": v(-15.7, 37.95) * mm});
            skLineSegment(sketch, "E47.3.11", {"start": v(3.56, 40.9) * mm, "end": v(3.74, 42.94) * mm});
            skLineSegment(sketch, "E47.3.12", {"start": v(-4.74, 14.57) * mm, "end": v(-5.35, 16.47) * mm});
            skArc(sketch, "E47.3.13", {"start": v(1.5, 17.25) * mm, "mid": v(-0.48, 17.3) * mm, "end": v(-2.46, 17.14) * mm});
            skLineSegment(sketch, "E47.3.14", {"start": v(-8.66, 15) * mm, "end": v(-7.66, 13.27) * mm});
            skLineSegment(sketch, "E47.3.15", {"start": v(1.33, 15.26) * mm, "end": v(1.5, 17.25) * mm});
            skLineSegment(sketch, "E47.3.16", {"start": v(-1.66, 11.57) * mm, "end": v(-1.4, 9.7) * mm});
            skArc(sketch, "E47.3.17", {"start": v(0.85, 9.76) * mm, "mid": v(-0.27, 9.8) * mm, "end": v(-1.4, 9.7) * mm});
            skArc(sketch, "E47.3.18", {"start": v(1.01, 11.64) * mm, "mid": v(-0.33, 11.68) * mm, "end": v(-1.66, 11.57) * mm});
            skLineSegment(sketch, "E47.3.19", {"start": v(-5.84, 10.12) * mm, "end": v(-4.9, 8.48) * mm});
            skArc(sketch, "E47.3.20", {"start": v(-4.47, 10.8) * mm, "mid": v(-5.17, 10.48) * mm, "end": v(-5.84, 10.12) * mm});
            skArc(sketch, "E47.3.21", {"start": v(-3.75, 9.05) * mm, "mid": v(-4.33, 8.79) * mm, "end": v(-4.9, 8.48) * mm});
            skLineSegment(sketch, "E47.3.22", {"start": v(0.85, 9.76) * mm, "end": v(1.01, 11.64) * mm});
            skLineSegment(sketch, "E47.3.23", {"start": v(-4.47, 10.8) * mm, "end": v(-3.75, 9.05) * mm});
            skArc(sketch, "E47.4.0", {"start": v(-16.48, 39.83) * mm, "mid": v(-26.98, 33.62) * mm, "end": v(-35.32, 24.71) * mm});
            skArc(sketch, "E47.4.1", {"start": v(-15.7, 37.95) * mm, "mid": v(-25.7, 32.03) * mm, "end": v(-33.65, 23.54) * mm});
            skArc(sketch, "E47.4.3", {"start": v(-14.98, 3.18) * mm, "mid": v(-15.23, 1.6) * mm, "end": v(-15.32, 0) * mm});
            skArc(sketch, "E47.4.5", {"start": v(-12.55, 8.78) * mm, "mid": v(-13.47, 7.29) * mm, "end": v(-14.22, 5.7) * mm});
            skLineSegment(sketch, "E47.4.6", {"start": v(-16.07, 6.44) * mm, "end": v(-14.22, 5.7) * mm});
            skArc(sketch, "E47.4.8", {"start": v(-16.94, 3.6) * mm, "mid": v(-17.22, 1.8) * mm, "end": v(-17.31, 0) * mm});
            skLineSegment(sketch, "E47.4.10", {"start": v(-42.73, 5.64) * mm, "end": v(-40.71, 5.38) * mm});
            skLineSegment(sketch, "E47.4.11", {"start": v(-33.65, 23.54) * mm, "end": v(-35.32, 24.71) * mm});
            skLineSegment(sketch, "E47.4.12", {"start": v(-14.98, 3.18) * mm, "end": v(-16.94, 3.6) * mm});
            skArc(sketch, "E47.4.13", {"start": v(-14.19, 9.93) * mm, "mid": v(-15.23, 8.24) * mm, "end": v(-16.07, 6.44) * mm});
            skLineSegment(sketch, "E47.4.14", {"start": v(-17.31, 0) * mm, "end": v(-15.32, 0) * mm});
            skLineSegment(sketch, "E47.4.15", {"start": v(-12.55, 8.78) * mm, "end": v(-14.19, 9.93) * mm});
            skLineSegment(sketch, "E47.4.16", {"start": v(-10.85, 4.35) * mm, "end": v(-9.1, 3.64) * mm});
            skArc(sketch, "E47.4.17", {"start": v(-8.03, 5.62) * mm, "mid": v(-8.62, 4.66) * mm, "end": v(-9.1, 3.64) * mm});
            skArc(sketch, "E47.4.18", {"start": v(-9.58, 6.7) * mm, "mid": v(-10.28, 5.56) * mm, "end": v(-10.85, 4.35) * mm});
            skLineSegment(sketch, "E47.4.19", {"start": v(-11.69, 0) * mm, "end": v(-9.8, 0) * mm});
            skArc(sketch, "E47.4.20", {"start": v(-11.59, 1.53) * mm, "mid": v(-11.66, 0.77) * mm, "end": v(-11.69, 0) * mm});
            skArc(sketch, "E47.4.21", {"start": v(-9.71, 1.28) * mm, "mid": v(-9.78, 0.64) * mm, "end": v(-9.8, 0) * mm});
            skLineSegment(sketch, "E47.4.22", {"start": v(-8.03, 5.62) * mm, "end": v(-9.58, 6.7) * mm});
            skLineSegment(sketch, "E47.4.23", {"start": v(-11.59, 1.53) * mm, "end": v(-9.71, 1.28) * mm});
            skArc(sketch, "E48.2.5.0", {"start": v(-42.73, 5.64) * mm, "mid": v(-42.6, -6.56) * mm, "end": v(-39.06, -18.23) * mm});
            skArc(sketch, "E48.4.5.0", {"start": v(-40.71, 5.38) * mm, "mid": v(-40.59, -6.25) * mm, "end": v(-37.21, -17.37) * mm});
            skArc(sketch, "E48.12.5.0", {"start": v(-10.25, -11.38) * mm, "mid": v(-9, -12.4) * mm, "end": v(-7.66, -13.27) * mm});
            skArc(sketch, "E48.19.5.0", {"start": v(-13.88, -6.48) * mm, "mid": v(-13.05, -8.03) * mm, "end": v(-12.04, -9.47) * mm});
            skLineSegment(sketch, "E48.23.5.0", {"start": v(-13.61, -10.7) * mm, "end": v(-12.04, -9.47) * mm});
            skArc(sketch, "E48.29.5.0", {"start": v(-11.58, -12.87) * mm, "mid": v(-10.18, -14) * mm, "end": v(-8.66, -15) * mm});
            skLineSegment(sketch, "E48.37.5.0", {"start": v(-26.26, -34.19) * mm, "end": v(-25.01, -32.57) * mm});
            skLineSegment(sketch, "E48.40.5.0", {"start": v(-37.21, -17.37) * mm, "end": v(-39.06, -18.23) * mm});
            skLineSegment(sketch, "E48.43.5.0", {"start": v(-10.25, -11.38) * mm, "end": v(-11.58, -12.87) * mm});
            skArc(sketch, "E48.46.5.0", {"start": v(-15.69, -7.32) * mm, "mid": v(-14.75, -9.07) * mm, "end": v(-13.61, -10.7) * mm});
            skLineSegment(sketch, "E48.50.5.0", {"start": v(-8.66, -15) * mm, "end": v(-7.66, -13.27) * mm});
            skLineSegment(sketch, "E48.53.5.0", {"start": v(-13.88, -6.48) * mm, "end": v(-15.69, -7.32) * mm});
            skLineSegment(sketch, "E48.56.5.0", {"start": v(-9.19, -7.22) * mm, "end": v(-7.7, -6.05) * mm});
            skArc(sketch, "E48.59.5.0", {"start": v(-8.88, -4.14) * mm, "mid": v(-8.34, -5.13) * mm, "end": v(-7.7, -6.05) * mm});
            skArc(sketch, "E48.63.5.0", {"start": v(-10.6, -4.94) * mm, "mid": v(-9.96, -6.12) * mm, "end": v(-9.19, -7.22) * mm});
            skLineSegment(sketch, "E48.67.5.0", {"start": v(-5.84, -10.12) * mm, "end": v(-4.9, -8.48) * mm});
            skArc(sketch, "E48.70.5.0", {"start": v(-7.12, -9.27) * mm, "mid": v(-6.5, -9.72) * mm, "end": v(-5.84, -10.12) * mm});
            skArc(sketch, "E48.74.5.0", {"start": v(-5.97, -7.77) * mm, "mid": v(-5.44, -8.14) * mm, "end": v(-4.9, -8.48) * mm});
            skLineSegment(sketch, "E48.78.5.0", {"start": v(-8.88, -4.14) * mm, "end": v(-10.6, -4.94) * mm});
            skLineSegment(sketch, "E48.81.5.0", {"start": v(-7.12, -9.27) * mm, "end": v(-5.97, -7.77) * mm});
            skSolve(sketch);
        }
        {
            var Q0;
            Q0 = qSketchRegion(id + "F6", true);
            extrude(context, id + "F7", {"entities" : qUnion([Q0]), "operationType" : NewBodyOperationType.REMOVE, "oppositeDirection" : true, "depth" : 25.4 * mm});
        }
        {
            var Q0;
            Q0=makeQuery(id+"F6.imprint","IMPRINT",FACE,{"disambiguationData":[TD([[makeQuery(id+"F6.imprint","IMPRINT",EDGE,{"derivedFrom":sQuery(id+"F6.wireOp",EDGE,"E25")}),1.0]])]});
            var sketch = newSketch(context, id + "F8", { "sketchPlane" : qUnion([Q0])});
            skCircle(sketch, "E49", {"center": v(4.73, -42.16) * mm, "radius": 2.75 * mm});
            skEllipse(sketch, "E50", {"center": v(0, -34.63) * mm, "majorRadius": 3.83 * mm, "minorRadius": 2.1 * mm, "majorAxis": v(0.62, -0.79)});
            skEllipse(sketch, "E51", {"center": v(12.04, -39.36) * mm, "majorRadius": 5.55 * mm, "minorRadius": 1.72 * mm, "majorAxis": v(0.58, -0.81)});
            skEllipse(sketch, "E52", {"center": v(-7.53, -46.89) * mm, "majorRadius": 6.67 * mm, "minorRadius": 1.97 * mm, "majorAxis": v(1, 0)});
            skEllipse(sketch, "E53", {"center": v(25.16, -41.73) * mm, "majorRadius": 4.72 * mm, "minorRadius": 1.84 * mm, "majorAxis": v(0.5, -0.87)});
            skEllipse(sketch, "E54", {"center": v(0, -4.95) * mm, "majorRadius": 1.72 * mm, "minorRadius": 1.4 * mm, "majorAxis": v(0, -1)});
            skEllipse(sketch, "E55.1.0", {"center": v(36.84, -29.96) * mm, "majorRadius": 6.67 * mm, "minorRadius": 1.97 * mm, "majorAxis": v(0.5, 0.87)});
            skEllipse(sketch, "E55.1.1", {"center": v(29.99, -17.31) * mm, "majorRadius": 3.83 * mm, "minorRadius": 2.1 * mm, "majorAxis": v(0.99, 0.14)});
            skCircle(sketch, "E55.1.2", {"center": v(38.87, -16.98) * mm, "radius": 2.75 * mm});
            skEllipse(sketch, "E55.1.3", {"center": v(48.72, 0.93) * mm, "majorRadius": 4.72 * mm, "minorRadius": 1.84 * mm, "majorAxis": v(1, 0)});
            skEllipse(sketch, "E55.1.4", {"center": v(40.1, -9.25) * mm, "majorRadius": 5.55 * mm, "minorRadius": 1.72 * mm, "majorAxis": v(1, 0.1)});
            skEllipse(sketch, "E55.1.5", {"center": v(4.28, -2.47) * mm, "majorRadius": 1.72 * mm, "minorRadius": 1.4 * mm, "majorAxis": v(0.87, -0.5)});
            skEllipse(sketch, "E55.2.0", {"center": v(44.37, 16.92) * mm, "majorRadius": 6.67 * mm, "minorRadius": 1.97 * mm, "majorAxis": v(-0.5, 0.87)});
            skEllipse(sketch, "E55.2.1", {"center": v(29.99, 17.31) * mm, "majorRadius": 3.83 * mm, "minorRadius": 2.1 * mm, "majorAxis": v(0.37, 0.93)});
            skCircle(sketch, "E55.2.2", {"center": v(34.14, 25.18) * mm, "radius": 2.75 * mm});
            skEllipse(sketch, "E55.2.3", {"center": v(23.55, 42.66) * mm, "majorRadius": 4.72 * mm, "minorRadius": 1.84 * mm, "majorAxis": v(0.5, 0.87)});
            skEllipse(sketch, "E55.2.4", {"center": v(28.06, 30.11) * mm, "majorRadius": 5.55 * mm, "minorRadius": 1.72 * mm, "majorAxis": v(0.41, 0.91)});
            skEllipse(sketch, "E55.2.5", {"center": v(4.28, 2.47) * mm, "majorRadius": 1.72 * mm, "minorRadius": 1.4 * mm, "majorAxis": v(0.87, 0.5)});
            skEllipse(sketch, "E55.3.0", {"center": v(7.53, 46.89) * mm, "majorRadius": 6.67 * mm, "minorRadius": 1.97 * mm, "majorAxis": v(-1, 0)});
            skEllipse(sketch, "E55.3.1", {"center": v(0, 34.63) * mm, "majorRadius": 3.83 * mm, "minorRadius": 2.1 * mm, "majorAxis": v(-0.62, 0.79)});
            skCircle(sketch, "E55.3.2", {"center": v(-4.73, 42.16) * mm, "radius": 2.75 * mm});
            skEllipse(sketch, "E55.3.3", {"center": v(-25.16, 41.73) * mm, "majorRadius": 4.72 * mm, "minorRadius": 1.84 * mm, "majorAxis": v(-0.5, 0.87)});
            skEllipse(sketch, "E55.3.4", {"center": v(-12.04, 39.36) * mm, "majorRadius": 5.55 * mm, "minorRadius": 1.72 * mm, "majorAxis": v(-0.58, 0.81)});
            skEllipse(sketch, "E55.3.5", {"center": v(0, 4.95) * mm, "majorRadius": 1.72 * mm, "minorRadius": 1.4 * mm, "majorAxis": v(0, 1)});
            skEllipse(sketch, "E55.4.0", {"center": v(-36.84, 29.96) * mm, "majorRadius": 6.67 * mm, "minorRadius": 1.97 * mm, "majorAxis": v(-0.5, -0.87)});
            skEllipse(sketch, "E55.4.1", {"center": v(-29.99, 17.31) * mm, "majorRadius": 3.83 * mm, "minorRadius": 2.1 * mm, "majorAxis": v(-0.99, -0.14)});
            skCircle(sketch, "E55.4.2", {"center": v(-38.87, 16.98) * mm, "radius": 2.75 * mm});
            skEllipse(sketch, "E55.4.3", {"center": v(-48.72, -0.93) * mm, "majorRadius": 4.72 * mm, "minorRadius": 1.84 * mm, "majorAxis": v(-1, 0)});
            skEllipse(sketch, "E55.4.4", {"center": v(-40.1, 9.25) * mm, "majorRadius": 5.55 * mm, "minorRadius": 1.72 * mm, "majorAxis": v(-1, -0.1)});
            skEllipse(sketch, "E55.4.5", {"center": v(-4.28, 2.47) * mm, "majorRadius": 1.72 * mm, "minorRadius": 1.4 * mm, "majorAxis": v(-0.87, 0.5)});
            skEllipse(sketch, "E55.5.0", {"center": v(-44.37, -16.92) * mm, "majorRadius": 6.67 * mm, "minorRadius": 1.97 * mm, "majorAxis": v(0.5, -0.87)});
            skEllipse(sketch, "E55.5.1", {"center": v(-29.99, -17.31) * mm, "majorRadius": 3.83 * mm, "minorRadius": 2.1 * mm, "majorAxis": v(-0.37, -0.93)});
            skCircle(sketch, "E55.5.2", {"center": v(-34.14, -25.18) * mm, "radius": 2.75 * mm});
            skEllipse(sketch, "E55.5.3", {"center": v(-23.55, -42.66) * mm, "majorRadius": 4.72 * mm, "minorRadius": 1.84 * mm, "majorAxis": v(-0.5, -0.87)});
            skEllipse(sketch, "E55.5.4", {"center": v(-28.06, -30.11) * mm, "majorRadius": 5.55 * mm, "minorRadius": 1.72 * mm, "majorAxis": v(-0.41, -0.91)});
            skEllipse(sketch, "E55.5.5", {"center": v(-4.28, -2.47) * mm, "majorRadius": 1.72 * mm, "minorRadius": 1.4 * mm, "majorAxis": v(-0.87, -0.5)});
            skPoint(sketch, "E55.center", {"position": v(0, 0) * mm});
            skSolve(sketch);
        }
        {
            var Q0;
            Q0 = qSketchRegion(id + "F8", true);
            extrude(context, id + "F9", {"entities" : qUnion([Q0]), "operationType" : NewBodyOperationType.REMOVE, "oppositeDirection" : true, "depth" : 25.4 * mm});
        }
        {
            var Q0;
            Q0=makeQuery(id+"F1.opExtrude","SWEPT_BODY",BODY,{"disambiguationData":[OSD([sQuery(id+"F0.wireOp",EDGE,"E1"),sQuery(id+"F0.wireOp",EDGE,"E2"),sQuery(id+"F0.wireOp",EDGE,"E3"),sQuery(id+"F0.wireOp",EDGE,"E4"),sQuery(id+"F0.wireOp",EDGE,"E5.top"),sQuery(id+"F0.wireOp",EDGE,"E5.left"),sQuery(id+"F0.wireOp",EDGE,"E5.right"),sQuery(id+"F0.wireOp",EDGE,"E6.bottom"),sQuery(id+"F0.wireOp",EDGE,"E6.top"),sQuery(id+"F0.wireOp",EDGE,"E6.left"),sQuery(id+"F0.wireOp",EDGE,"E6.right"),sQuery(id+"F0.wireOp",EDGE,"E9.trimOffspring"),sQuery(id+"F0.wireOp",EDGE,"E10.1.0"),sQuery(id+"F0.wireOp",EDGE,"E10.1.1"),sQuery(id+"F0.wireOp",EDGE,"E10.1.2"),sQuery(id+"F0.wireOp",EDGE,"E10.1.3"),sQuery(id+"F0.wireOp",EDGE,"E10.1.4"),sQuery(id+"F0.wireOp",EDGE,"E10.1.5"),sQuery(id+"F0.wireOp",EDGE,"E10.1.7"),sQuery(id+"F0.wireOp",EDGE,"E10.1.9"),sQuery(id+"F0.wireOp",EDGE,"E10.1.11"),sQuery(id+"F0.wireOp",EDGE,"E10.1.12"),sQuery(id+"F0.wireOp",EDGE,"E10.1.13"),sQuery(id+"F0.wireOp",EDGE,"E10.1.14"),sQuery(id+"F0.wireOp",EDGE,"E10.2.0"),sQuery(id+"F0.wireOp",EDGE,"E10.2.1"),sQuery(id+"F0.wireOp",EDGE,"E10.2.2"),sQuery(id+"F0.wireOp",EDGE,"E10.2.3"),sQuery(id+"F0.wireOp",EDGE,"E10.2.4"),sQuery(id+"F0.wireOp",EDGE,"E10.2.5"),sQuery(id+"F0.wireOp",EDGE,"E10.2.7"),sQuery(id+"F0.wireOp",EDGE,"E10.2.9"),sQuery(id+"F0.wireOp",EDGE,"E10.2.11"),sQuery(id+"F0.wireOp",EDGE,"E10.2.12"),sQuery(id+"F0.wireOp",EDGE,"E10.2.13"),sQuery(id+"F0.wireOp",EDGE,"E10.2.14"),sQuery(id+"F0.wireOp",EDGE,"E10.3.0"),sQuery(id+"F0.wireOp",EDGE,"E10.3.1"),sQuery(id+"F0.wireOp",EDGE,"E10.3.2"),sQuery(id+"F0.wireOp",EDGE,"E10.3.3"),sQuery(id+"F0.wireOp",EDGE,"E10.3.4"),sQuery(id+"F0.wireOp",EDGE,"E10.3.5"),sQuery(id+"F0.wireOp",EDGE,"E10.3.7"),sQuery(id+"F0.wireOp",EDGE,"E10.3.9"),sQuery(id+"F0.wireOp",EDGE,"E10.3.11"),sQuery(id+"F0.wireOp",EDGE,"E10.3.12"),sQuery(id+"F0.wireOp",EDGE,"E10.3.13"),sQuery(id+"F0.wireOp",EDGE,"E10.3.14"),sQuery(id+"F0.wireOp",EDGE,"E10.4.0"),sQuery(id+"F0.wireOp",EDGE,"E10.4.1"),sQuery(id+"F0.wireOp",EDGE,"E10.4.2"),sQuery(id+"F0.wireOp",EDGE,"E10.4.3"),sQuery(id+"F0.wireOp",EDGE,"E10.4.4"),sQuery(id+"F0.wireOp",EDGE,"E10.4.5"),sQuery(id+"F0.wireOp",EDGE,"E10.4.7"),sQuery(id+"F0.wireOp",EDGE,"E10.4.9"),sQuery(id+"F0.wireOp",EDGE,"E10.4.11"),sQuery(id+"F0.wireOp",EDGE,"E10.4.12"),sQuery(id+"F0.wireOp",EDGE,"E10.4.13"),sQuery(id+"F0.wireOp",EDGE,"E10.4.14"),sQuery(id+"F0.wireOp",EDGE,"E10.5.0"),sQuery(id+"F0.wireOp",EDGE,"E10.5.1"),sQuery(id+"F0.wireOp",EDGE,"E10.5.2"),sQuery(id+"F0.wireOp",EDGE,"E10.5.3"),sQuery(id+"F0.wireOp",EDGE,"E10.5.4"),sQuery(id+"F0.wireOp",EDGE,"E10.5.5"),sQuery(id+"F0.wireOp",EDGE,"E10.5.7"),sQuery(id+"F0.wireOp",EDGE,"E10.5.9"),sQuery(id+"F0.wireOp",EDGE,"E10.5.11"),sQuery(id+"F0.wireOp",EDGE,"E10.5.12"),sQuery(id+"F0.wireOp",EDGE,"E10.5.13"),sQuery(id+"F0.wireOp",EDGE,"E10.5.14")])]});
            var Q1;
            Q1=sQuery(id+"F6.wireOp",VERTEX,"E25.center");
            transform(context, id + "F10", {"entities" : qUnion([Q0]), "transformType" : TransformType.SCALE_UNIFORMLY, "scale" : .5, "scalePoint" : qUnion([Q1]), "makeCopy" : false});
        }
        {
            var Q0;
            Q0=makeQuery(id+"F1.opExtrude","SWEPT_BODY",BODY,{"disambiguationData":[OSD([sQuery(id+"F0.wireOp",EDGE,"E1"),sQuery(id+"F0.wireOp",EDGE,"E2"),sQuery(id+"F0.wireOp",EDGE,"E3"),sQuery(id+"F0.wireOp",EDGE,"E4"),sQuery(id+"F0.wireOp",EDGE,"E5.top"),sQuery(id+"F0.wireOp",EDGE,"E5.left"),sQuery(id+"F0.wireOp",EDGE,"E5.right"),sQuery(id+"F0.wireOp",EDGE,"E6.bottom"),sQuery(id+"F0.wireOp",EDGE,"E6.top"),sQuery(id+"F0.wireOp",EDGE,"E6.left"),sQuery(id+"F0.wireOp",EDGE,"E6.right"),sQuery(id+"F0.wireOp",EDGE,"E9.trimOffspring"),sQuery(id+"F0.wireOp",EDGE,"E10.1.0"),sQuery(id+"F0.wireOp",EDGE,"E10.1.1"),sQuery(id+"F0.wireOp",EDGE,"E10.1.2"),sQuery(id+"F0.wireOp",EDGE,"E10.1.3"),sQuery(id+"F0.wireOp",EDGE,"E10.1.4"),sQuery(id+"F0.wireOp",EDGE,"E10.1.5"),sQuery(id+"F0.wireOp",EDGE,"E10.1.7"),sQuery(id+"F0.wireOp",EDGE,"E10.1.9"),sQuery(id+"F0.wireOp",EDGE,"E10.1.11"),sQuery(id+"F0.wireOp",EDGE,"E10.1.12"),sQuery(id+"F0.wireOp",EDGE,"E10.1.13"),sQuery(id+"F0.wireOp",EDGE,"E10.1.14"),sQuery(id+"F0.wireOp",EDGE,"E10.2.0"),sQuery(id+"F0.wireOp",EDGE,"E10.2.1"),sQuery(id+"F0.wireOp",EDGE,"E10.2.2"),sQuery(id+"F0.wireOp",EDGE,"E10.2.3"),sQuery(id+"F0.wireOp",EDGE,"E10.2.4"),sQuery(id+"F0.wireOp",EDGE,"E10.2.5"),sQuery(id+"F0.wireOp",EDGE,"E10.2.7"),sQuery(id+"F0.wireOp",EDGE,"E10.2.9"),sQuery(id+"F0.wireOp",EDGE,"E10.2.11"),sQuery(id+"F0.wireOp",EDGE,"E10.2.12"),sQuery(id+"F0.wireOp",EDGE,"E10.2.13"),sQuery(id+"F0.wireOp",EDGE,"E10.2.14"),sQuery(id+"F0.wireOp",EDGE,"E10.3.0"),sQuery(id+"F0.wireOp",EDGE,"E10.3.1"),sQuery(id+"F0.wireOp",EDGE,"E10.3.2"),sQuery(id+"F0.wireOp",EDGE,"E10.3.3"),sQuery(id+"F0.wireOp",EDGE,"E10.3.4"),sQuery(id+"F0.wireOp",EDGE,"E10.3.5"),sQuery(id+"F0.wireOp",EDGE,"E10.3.7"),sQuery(id+"F0.wireOp",EDGE,"E10.3.9"),sQuery(id+"F0.wireOp",EDGE,"E10.3.11"),sQuery(id+"F0.wireOp",EDGE,"E10.3.12"),sQuery(id+"F0.wireOp",EDGE,"E10.3.13"),sQuery(id+"F0.wireOp",EDGE,"E10.3.14"),sQuery(id+"F0.wireOp",EDGE,"E10.4.0"),sQuery(id+"F0.wireOp",EDGE,"E10.4.1"),sQuery(id+"F0.wireOp",EDGE,"E10.4.2"),sQuery(id+"F0.wireOp",EDGE,"E10.4.3"),sQuery(id+"F0.wireOp",EDGE,"E10.4.4"),sQuery(id+"F0.wireOp",EDGE,"E10.4.5"),sQuery(id+"F0.wireOp",EDGE,"E10.4.7"),sQuery(id+"F0.wireOp",EDGE,"E10.4.9"),sQuery(id+"F0.wireOp",EDGE,"E10.4.11"),sQuery(id+"F0.wireOp",EDGE,"E10.4.12"),sQuery(id+"F0.wireOp",EDGE,"E10.4.13"),sQuery(id+"F0.wireOp",EDGE,"E10.4.14"),sQuery(id+"F0.wireOp",EDGE,"E10.5.0"),sQuery(id+"F0.wireOp",EDGE,"E10.5.1"),sQuery(id+"F0.wireOp",EDGE,"E10.5.2"),sQuery(id+"F0.wireOp",EDGE,"E10.5.3"),sQuery(id+"F0.wireOp",EDGE,"E10.5.4"),sQuery(id+"F0.wireOp",EDGE,"E10.5.5"),sQuery(id+"F0.wireOp",EDGE,"E10.5.7"),sQuery(id+"F0.wireOp",EDGE,"E10.5.9"),sQuery(id+"F0.wireOp",EDGE,"E10.5.11"),sQuery(id+"F0.wireOp",EDGE,"E10.5.12"),sQuery(id+"F0.wireOp",EDGE,"E10.5.13"),sQuery(id+"F0.wireOp",EDGE,"E10.5.14")])]});
            var Q1;
            Q1=makeQuery(id+"F1.opExtrude","SWEPT_EDGE",EDGE,{"disambiguationData":[OSD([sQuery(id+"F0.wireOp",EDGE,"E10.3.3"),sQuery(id+"F0.wireOp",EDGE,"E10.3.11")])]});
            var Q2;
            Q2=makeQuery(id+"F1.opExtrude","SWEPT_EDGE",EDGE,{"disambiguationData":[OSD([sQuery(id+"F0.wireOp",EDGE,"E10.3.3"),sQuery(id+"F0.wireOp",EDGE,"E10.3.11")])]});
            transform(context, id + "F11", {"entities" : qUnion([Q0]), "transformType" : TransformType.TRANSLATION_DISTANCE, "transformDirection" : qUnion([Q2]), "distance" : 76.2 * mm, "makeCopy" : true});
        }
    });
